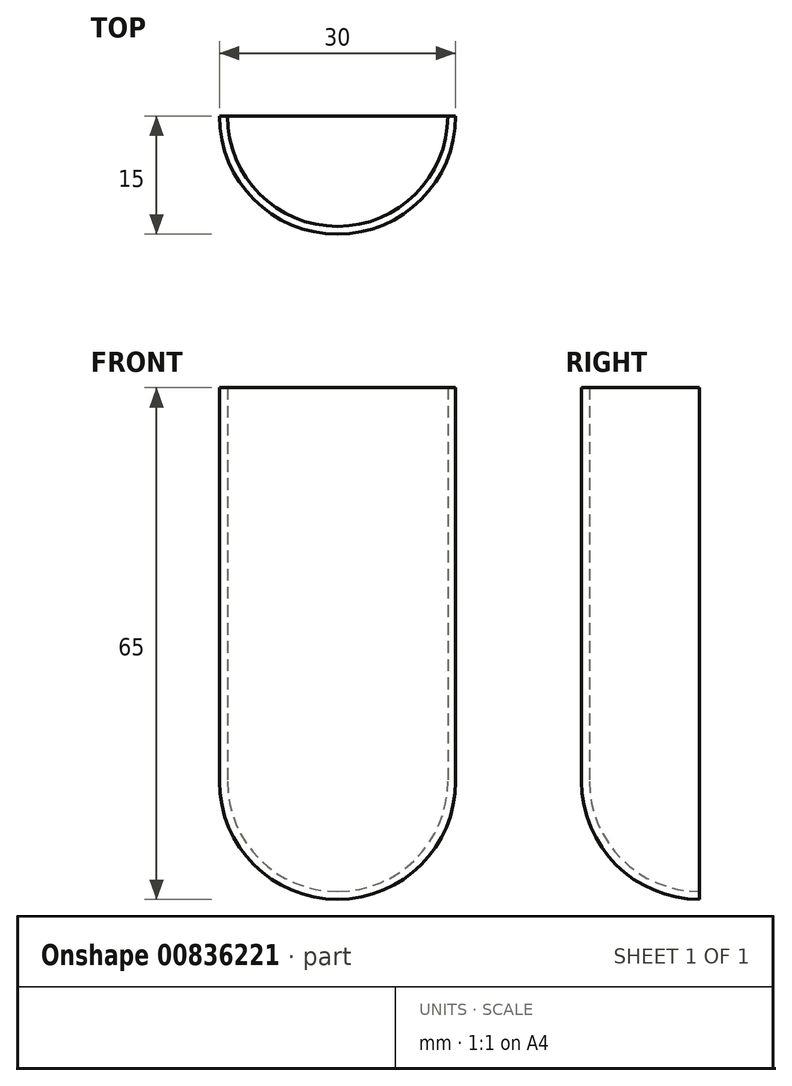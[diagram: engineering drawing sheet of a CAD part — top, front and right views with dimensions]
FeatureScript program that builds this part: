
annotation { "Feature Type Name" : "Feature", "Feature Type Description" : "" }
export const myFeature = defineFeature(function(context is Context, id is Id, definition is map)
    precondition{}
    {
        {
            var Q0;
            Q0=qCreatedBy(makeId("Front.planeOp"),FACE);
            var sketch = newSketch(context, id + "F0", { "sketchPlane" : qUnion([Q0])});
            skArc(sketch, "E0", {"start": v(-15, 0) * mm, "mid": v(-10.6, -10.6) * mm, "end": v(0, -15) * mm});
            skLineSegment(sketch, "E1", {"start": v(-15, 0) * mm, "end": v(-15, 50) * mm});
            skLineSegment(sketch, "E2", {"start": v(-15, 50) * mm, "end": v(0, 50) * mm});
            skLineSegment(sketch, "E3", {"start": v(0, -15) * mm, "end": v(0, 50) * mm});
            skSolve(sketch);
        }
        {
            var Q0;
            Q0 = qSketchRegion(id + "F0", true);
            var Q1;
            Q1=sQuery(id+"F0.wireOp",EDGE,"E3");
            revolve(context, id + "F1", {"surfaceOperationType" : NewSurfaceOperationType.NEW, "entities" : qUnion([Q0]), "axis" : qUnion([Q1]), "revolveType" : RevolveType.FULL});
        }
        {
            var Q0;
            Q0=qCreatedBy(makeId("Top.planeOp"),FACE);
            cPlane(context, id + "F2", {"entities" : qUnion([Q0]), "cplaneType" : CPlaneType.OFFSET, "offset" : 50 * mm, "width" : 150 * mm, "height" : 150 * mm});
        }
        {
            var Q0;
            Q0=qCreatedBy(id+"F2.planeOp",FACE);
            var sketch = newSketch(context, id + "F3", { "sketchPlane" : qUnion([Q0])});
            skArc(sketch, "E4.0", {"start": v(15, 0) * mm, "mid": v(0, 15) * mm, "end": v(-15, 0) * mm});
            skLineSegment(sketch, "E5", {"start": v(-15, 0) * mm, "end": v(15, 0) * mm});
            skSolve(sketch);
        }
        {
            var Q0;
            Q0 = qSketchRegion(id + "F3", true);
            extrude(context, id + "F4", {"entities" : qUnion([Q0]), "operationType" : NewBodyOperationType.REMOVE, "endBound" : BoundingType.THROUGH_ALL, "oppositeDirection" : true, "depth" : 25 * mm, "offsetDistance" : 25 * mm});
        }
        {
            var Q0;
            Q0=makeQuery(id+"F4.boolean.opBoolean","COPY",FACE,{"derivedFrom":makeQuery(id+"F4.opExtrude","SWEPT_FACE",FACE,{"disambiguationData":[OSD([sQuery(id+"F3.wireOp",EDGE,"E5")])]})});
            var Q1;
            Q1=makeQuery(id+"F1.opRevolve","SWEPT_FACE",FACE,{"disambiguationData":[OSD([sQuery(id+"F0.wireOp",EDGE,"E2")])]});
            shell(context, id + "F5", {"entities" : qUnion([Q0, Q1]), "thickness" : 1 * mm});
        }
    });
